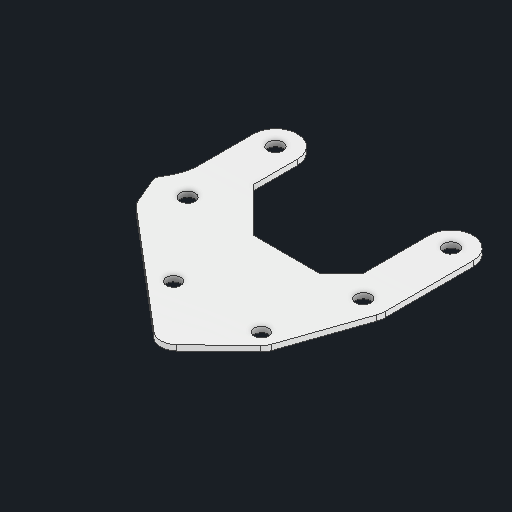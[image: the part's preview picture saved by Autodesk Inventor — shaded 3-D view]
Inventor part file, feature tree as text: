
AUTODESK INVENTOR PART (.ipt)
format: ipt  version: 2025 (Build 290162000, 162)  size: 145,408 bytes
history: native  units: in
note: dims shown in document units (in); Inventor stores cm internally (conversion verified against a paired STEP export)
features: other x3, extrude x1, sketch x1
ambient origin geometry x8: Origin, YZ Plane, XZ Plane, XY Plane, X Axis, Y Axis, Z Axis, Center Point
bodies: Solid1 (feature_tree)
feature tree (5):
  other  "Blocks"
  extrude  "Extrusion1"  Depth=0.25in
  sketch  "Sketch1"  dims[d0=0.164in d1=0.375in d2=0.5in d3=0.5in d4=0.25in d5=0.25in d6=0.164in d7=0.1875in d9=0.125in d10=0.0625in d11=0.0in d12=1.911in d14=0.125in d15=0.5in d16=1.0in d17=1.9106in d18=0.25in]
  other  "main"
  other  "main:1"
